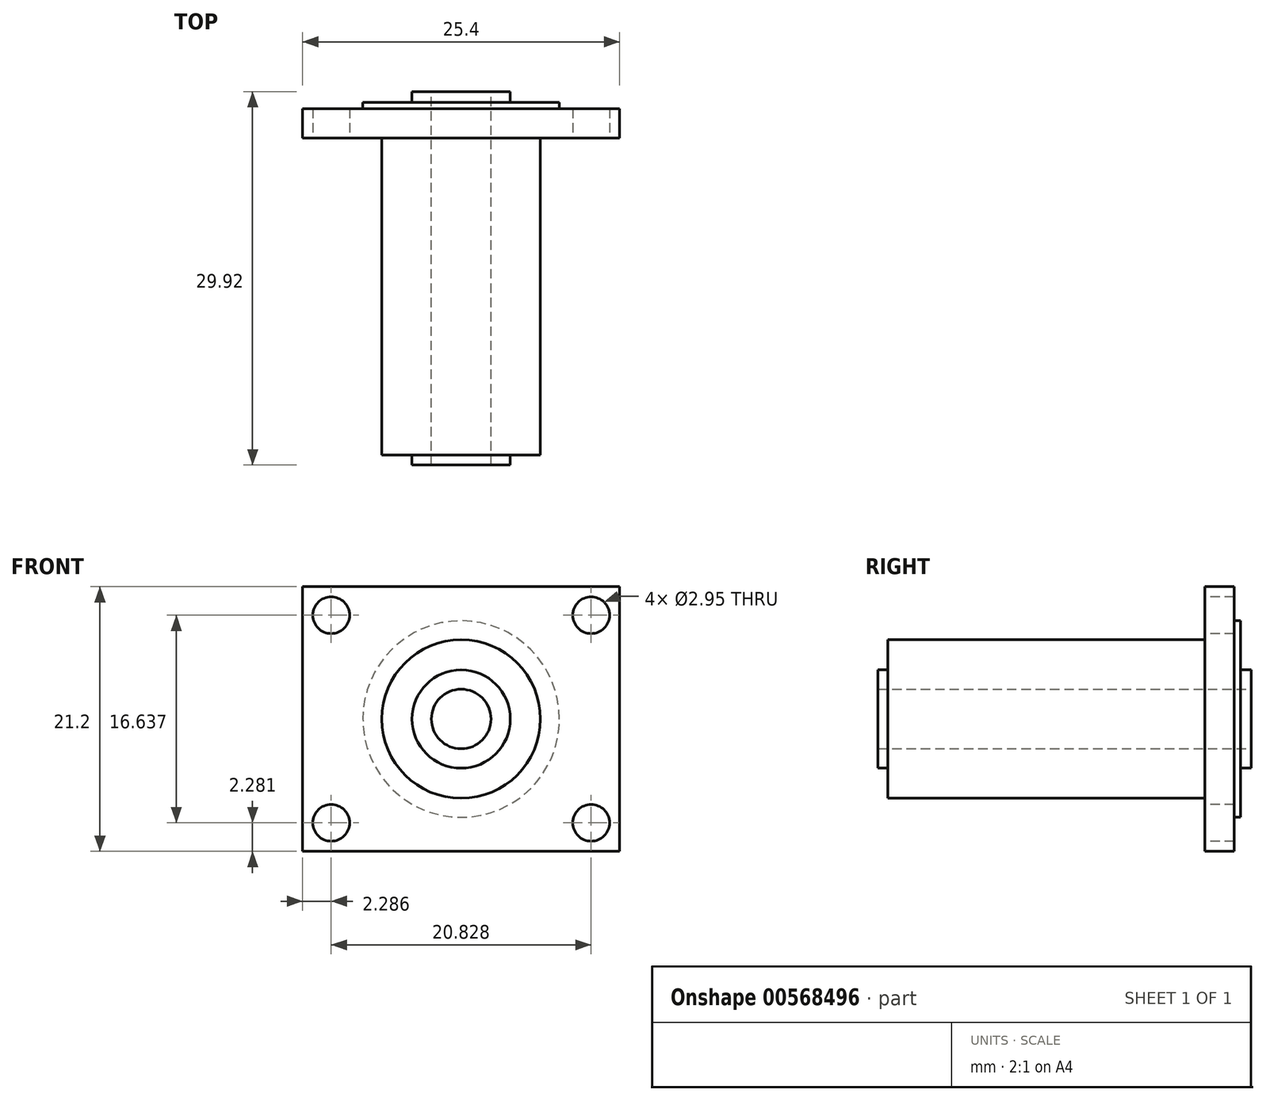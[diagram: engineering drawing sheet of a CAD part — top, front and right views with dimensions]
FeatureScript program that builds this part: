
annotation { "Feature Type Name" : "Feature", "Feature Type Description" : "" }
export const myFeature = defineFeature(function(context is Context, id is Id, definition is map)
    precondition{}
    {
        {
            var Q0;
            Q0=qCreatedBy(makeId("Front.planeOp"),FACE);
            var sketch = newSketch(context, id + "F0", { "sketchPlane" : qUnion([Q0])});
            skCircle(sketch, "E0", {"center": v(0, 0) * mm, "radius": 6.35 * mm});
            skCircle(sketch, "E1", {"center": v(0, 0) * mm, "radius": 2.39 * mm});
            skSolve(sketch);
        }
        {
            var Q0;
            Q0 = qSketchRegion(id + "F0", true);
            extrude(context, id + "F1", {"entities" : qUnion([Q0]), "depth" : 25.4 * mm, "offsetDistance" : 25.4 * mm});
        }
        {
            var Q0;
            Q0=makeQuery(id+"F1.opExtrude","CAP_FACE",FACE,{"disambiguationData":[OSD([sQuery(id+"F0.wireOp",EDGE,"E0"),sQuery(id+"F0.wireOp",EDGE,"E1")])],"isStart":true});
            var sketch = newSketch(context, id + "F2", { "sketchPlane" : qUnion([Q0])});
            skLineSegment(sketch, "E2.bottom", {"start": v(12.7, 10.6) * mm, "end": v(-12.7, 10.6) * mm});
            skLineSegment(sketch, "E2.top", {"start": v(12.7, -10.6) * mm, "end": v(-12.7, -10.6) * mm});
            skLineSegment(sketch, "E2.left", {"start": v(12.7, 10.6) * mm, "end": v(12.7, -10.6) * mm});
            skLineSegment(sketch, "E2.right", {"start": v(-12.7, 10.6) * mm, "end": v(-12.7, -10.6) * mm});
            skPoint(sketch, "E2.middle", {"position": v(0, 0) * mm});
            skSolve(sketch);
        }
        {
            var Q0;
            Q0 = qSketchRegion(id + "F2", true);
            extrude(context, id + "F3", {"entities" : qUnion([Q0]), "operationType" : NewBodyOperationType.ADD, "depth" : 2.36 * mm, "offsetDistance" : 25.4 * mm});
        }
        {
            var Q0;
            Q0=makeQuery(id+"F3.opExtrude","CAP_FACE",FACE,{"disambiguationData":[OSD([sQuery(id+"F2.wireOp",EDGE,"E2.bottom"),sQuery(id+"F2.wireOp",EDGE,"E2.top"),sQuery(id+"F2.wireOp",EDGE,"E2.left"),sQuery(id+"F2.wireOp",EDGE,"E2.right")])],"isStart":false});
            var sketch = newSketch(context, id + "F4", { "sketchPlane" : qUnion([Q0])});
            skCircle(sketch, "E3", {"center": v(0, 0) * mm, "radius": 7.87 * mm});
            skSolve(sketch);
        }
        {
            var Q0;
            Q0 = qSketchRegion(id + "F4", true);
            extrude(context, id + "F5", {"entities" : qUnion([Q0]), "operationType" : NewBodyOperationType.ADD, "depth" : 0.5 * mm, "offsetDistance" : 25.4 * mm});
        }
        {
            var Q0;
            Q0=makeQuery(id+"F5.opExtrude","CAP_FACE",FACE,{"disambiguationData":[OSD([sQuery(id+"F4.wireOp",EDGE,"E3")])],"isStart":false});
            var sketch = newSketch(context, id + "F6", { "sketchPlane" : qUnion([Q0])});
            skCircle(sketch, "E4", {"center": v(0, 0) * mm, "radius": 2.39 * mm});
            skSolve(sketch);
        }
        {
            var Q0;
            Q0 = qSketchRegion(id + "F6", true);
            extrude(context, id + "F7", {"entities" : qUnion([Q0]), "operationType" : NewBodyOperationType.REMOVE, "endBound" : BoundingType.THROUGH_ALL, "oppositeDirection" : true, "depth" : 25.4 * mm, "offsetDistance" : 25.4 * mm});
        }
        {
            var Q0;
            Q0=makeQuery(id+"F5.opExtrude","CAP_FACE",FACE,{"disambiguationData":[OSD([sQuery(id+"F4.wireOp",EDGE,"E3")])],"isStart":false});
            var sketch = newSketch(context, id + "F8", { "sketchPlane" : qUnion([Q0])});
            skCircle(sketch, "E5", {"center": v(0, 0) * mm, "radius": 3.94 * mm});
            skSolve(sketch);
        }
        {
            var Q0;
            Q0=makeQuery(id+"F8.imprint","IMPRINT",FACE,{"disambiguationData":[TD([[makeQuery(id+"F8.imprint","IMPRINT",EDGE,{"derivedFrom":sQuery(id+"F8.wireOp",EDGE,"E5")}),1.0]])]});
            extrude(context, id + "F9", {"entities" : qUnion([Q0]), "operationType" : NewBodyOperationType.ADD, "depth" : 0.86 * mm, "offsetDistance" : 25.4 * mm});
        }
        {
            var Q0;
            Q0=makeQuery(id+"F1.opExtrude","CAP_FACE",FACE,{"disambiguationData":[OSD([sQuery(id+"F0.wireOp",EDGE,"E0"),sQuery(id+"F0.wireOp",EDGE,"E1")])],"isStart":false});
            var sketch = newSketch(context, id + "F10", { "sketchPlane" : qUnion([Q0])});
            skCircle(sketch, "E6", {"center": v(0, 0) * mm, "radius": 3.94 * mm});
            skSolve(sketch);
        }
        {
            var Q0;
            Q0=makeQuery(id+"F10.imprint","IMPRINT",FACE,{"disambiguationData":[TD([[makeQuery(id+"F10.imprint","IMPRINT",EDGE,{"derivedFrom":sQuery(id+"F10.wireOp",EDGE,"E6")}),1.0]])]});
            extrude(context, id + "F11", {"entities" : qUnion([Q0]), "operationType" : NewBodyOperationType.ADD, "depth" : 0.79 * mm, "offsetDistance" : 25.4 * mm});
        }
        {
            var Q0;
            {var subQ0=sQuery(id+"F2.wireOp",EDGE,"E2.left");var subQ1=sQuery(id+"F2.wireOp",EDGE,"E2.top");var subQ2=sQuery(id+"F2.wireOp",EDGE,"E2.bottom");var subQ3=sQuery(id+"F2.wireOp",EDGE,"E2.right");Q0=makeQuery(id+"F3.boolean.opBoolean","SPLIT",FACE,{"disambiguationData":[TD([makeQuery(id+"F1.opExtrude","SWEPT_FACE",FACE,{"disambiguationData":[OSD([sQuery(id+"F0.wireOp",EDGE,"E0")])]})])],"derivedFrom":makeQuery(id+"F3.opExtrude","CAP_FACE",FACE,{"disambiguationData":[OSD([subQ2,subQ1,subQ0,subQ3])],"isStart":true})});}
            var sketch = newSketch(context, id + "F12", { "sketchPlane" : qUnion([Q0])});
            skCircle(sketch, "E7", {"center": v(-10.41, 8.32) * mm, "radius": 1.47 * mm});
            skCircle(sketch, "E8.1.0.0", {"center": v(10.41, 8.32) * mm, "radius": 1.47 * mm});
            skLineSegment(sketch, "E8.direction1", {"start": v(-10.41, 8.32) * mm, "end": v(10.41, 8.32) * mm, "construction": true});
            skCircle(sketch, "E9", {"center": v(-10.41, -8.32) * mm, "radius": 1.47 * mm});
            skCircle(sketch, "E10", {"center": v(10.41, -8.32) * mm, "radius": 1.47 * mm});
            skSolve(sketch);
        }
        {
            var Q0;
            Q0 = qSketchRegion(id + "F12", true);
            extrude(context, id + "F13", {"entities" : qUnion([Q0]), "operationType" : NewBodyOperationType.REMOVE, "endBound" : BoundingType.THROUGH_ALL, "oppositeDirection" : true, "depth" : 25.4 * mm, "offsetDistance" : 25.4 * mm});
        }
    });
